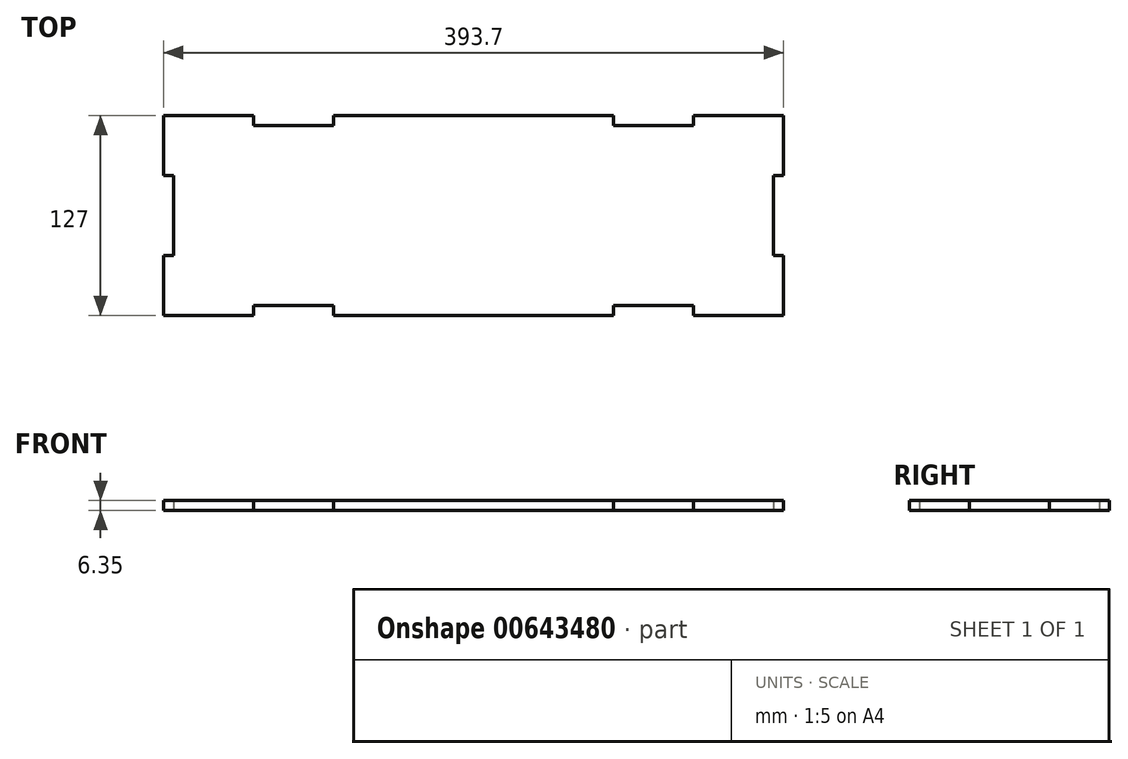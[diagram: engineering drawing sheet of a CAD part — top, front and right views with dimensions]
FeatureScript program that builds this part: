
annotation { "Feature Type Name" : "Feature", "Feature Type Description" : "" }
export const myFeature = defineFeature(function(context is Context, id is Id, definition is map)
    precondition{}
    {
        {
            var Q0;
            Q0=qCreatedBy(makeId("Top.planeOp"),FACE);
            var sketch = newSketch(context, id + "F0", { "sketchPlane" : qUnion([Q0])});
            skLineSegment(sketch, "E0.bottom", {"start": v(-176.11, 62.4) * mm, "end": v(204.89, 62.4) * mm});
            skLineSegment(sketch, "E0.top", {"start": v(-176.11, -64.6) * mm, "end": v(204.89, -64.6) * mm});
            skLineSegment(sketch, "E0.left", {"start": v(-176.11, 62.4) * mm, "end": v(-176.11, -64.6) * mm});
            skLineSegment(sketch, "E0.right", {"start": v(204.89, 62.4) * mm, "end": v(204.89, -64.6) * mm});
            skLineSegment(sketch, "E1.bottom", {"start": v(-125.31, 62.4) * mm, "end": v(-74.51, 62.4) * mm});
            skLineSegment(sketch, "E1.top", {"start": v(-125.31, 56.05) * mm, "end": v(-74.51, 56.05) * mm});
            skLineSegment(sketch, "E1.left", {"start": v(-125.31, 62.4) * mm, "end": v(-125.31, 56.05) * mm});
            skLineSegment(sketch, "E1.right", {"start": v(-74.51, 62.4) * mm, "end": v(-74.51, 56.05) * mm});
            skLineSegment(sketch, "E2.bottom", {"start": v(103.29, 62.4) * mm, "end": v(154.09, 62.4) * mm});
            skLineSegment(sketch, "E2.top", {"start": v(103.29, 56.05) * mm, "end": v(154.09, 56.05) * mm});
            skLineSegment(sketch, "E2.left", {"start": v(103.29, 62.4) * mm, "end": v(103.29, 56.05) * mm});
            skLineSegment(sketch, "E2.right", {"start": v(154.09, 62.4) * mm, "end": v(154.09, 56.05) * mm});
            skLineSegment(sketch, "E3.bottom", {"start": v(-125.31, -64.6) * mm, "end": v(-74.51, -64.6) * mm});
            skLineSegment(sketch, "E3.top", {"start": v(-125.31, -58.25) * mm, "end": v(-74.51, -58.25) * mm});
            skLineSegment(sketch, "E3.left", {"start": v(-125.31, -64.6) * mm, "end": v(-125.31, -58.25) * mm});
            skLineSegment(sketch, "E3.right", {"start": v(-74.51, -64.6) * mm, "end": v(-74.51, -58.25) * mm});
            skLineSegment(sketch, "E4.bottom", {"start": v(103.29, -64.6) * mm, "end": v(154.09, -64.6) * mm});
            skLineSegment(sketch, "E4.top", {"start": v(103.29, -58.25) * mm, "end": v(154.09, -58.25) * mm});
            skLineSegment(sketch, "E4.left", {"start": v(103.29, -64.6) * mm, "end": v(103.29, -58.25) * mm});
            skLineSegment(sketch, "E4.right", {"start": v(154.09, -64.6) * mm, "end": v(154.09, -58.25) * mm});
            skLineSegment(sketch, "E5.bottom", {"start": v(204.89, 62.4) * mm, "end": v(211.24, 62.4) * mm});
            skLineSegment(sketch, "E5.top", {"start": v(204.89, 24.3) * mm, "end": v(211.24, 24.3) * mm});
            skLineSegment(sketch, "E5.left", {"start": v(204.89, 62.4) * mm, "end": v(204.89, 24.3) * mm});
            skLineSegment(sketch, "E5.right", {"start": v(211.24, 62.4) * mm, "end": v(211.24, 24.3) * mm});
            skLineSegment(sketch, "E6.bottom", {"start": v(204.89, -64.6) * mm, "end": v(211.24, -64.6) * mm});
            skLineSegment(sketch, "E6.top", {"start": v(204.89, -26.5) * mm, "end": v(211.24, -26.5) * mm});
            skLineSegment(sketch, "E6.left", {"start": v(204.89, -64.6) * mm, "end": v(204.89, -26.5) * mm});
            skLineSegment(sketch, "E6.right", {"start": v(211.24, -64.6) * mm, "end": v(211.24, -26.5) * mm});
            skLineSegment(sketch, "E7.bottom", {"start": v(-176.11, 62.4) * mm, "end": v(-182.46, 62.4) * mm});
            skLineSegment(sketch, "E7.top", {"start": v(-176.11, 24.3) * mm, "end": v(-182.46, 24.3) * mm});
            skLineSegment(sketch, "E7.left", {"start": v(-176.11, 62.4) * mm, "end": v(-176.11, 24.3) * mm});
            skLineSegment(sketch, "E7.right", {"start": v(-182.46, 62.4) * mm, "end": v(-182.46, 24.3) * mm});
            skLineSegment(sketch, "E8.bottom", {"start": v(-176.11, -64.6) * mm, "end": v(-182.46, -64.6) * mm});
            skLineSegment(sketch, "E8.top", {"start": v(-176.11, -26.5) * mm, "end": v(-182.46, -26.5) * mm});
            skLineSegment(sketch, "E8.left", {"start": v(-176.11, -64.6) * mm, "end": v(-176.11, -26.5) * mm});
            skLineSegment(sketch, "E8.right", {"start": v(-182.46, -64.6) * mm, "end": v(-182.46, -26.5) * mm});
            skSolve(sketch);
        }
        {
            var Q0;
            Q0=makeQuery(id+"F0.imprint","IMPRINT",FACE,{"disambiguationData":[TD([[makeQuery(id+"F0.imprint","IMPRINT",EDGE,{"derivedFrom":sQuery(id+"F0.wireOp",EDGE,"E0.bottom")}),-1.0]])]});
            var Q1;
            Q1=makeQuery(id+"F0.imprint","IMPRINT",FACE,{"disambiguationData":[TD([[makeQuery(id+"F0.imprint","IMPRINT",EDGE,{"derivedFrom":sQuery(id+"F0.wireOp",EDGE,"E7.bottom")}),1.0]])]});
            var Q2;
            Q2=makeQuery(id+"F0.imprint","IMPRINT",FACE,{"disambiguationData":[TD([[makeQuery(id+"F0.imprint","IMPRINT",EDGE,{"derivedFrom":sQuery(id+"F0.wireOp",EDGE,"E8.bottom")}),-1.0]])]});
            var Q3;
            Q3=makeQuery(id+"F0.imprint","IMPRINT",FACE,{"disambiguationData":[TD([[makeQuery(id+"F0.imprint","IMPRINT",EDGE,{"derivedFrom":sQuery(id+"F0.wireOp",EDGE,"E5.bottom")}),-1.0]])]});
            var Q4;
            Q4=makeQuery(id+"F0.imprint","IMPRINT",FACE,{"disambiguationData":[TD([[makeQuery(id+"F0.imprint","IMPRINT",EDGE,{"derivedFrom":sQuery(id+"F0.wireOp",EDGE,"E6.bottom")}),1.0]])]});
            extrude(context, id + "F1", {"entities" : qUnion([Q0, Q1, Q2, Q3, Q4]), "depth" : 6.35 * mm, "offsetDistance" : 25.4 * mm});
        }
    });
